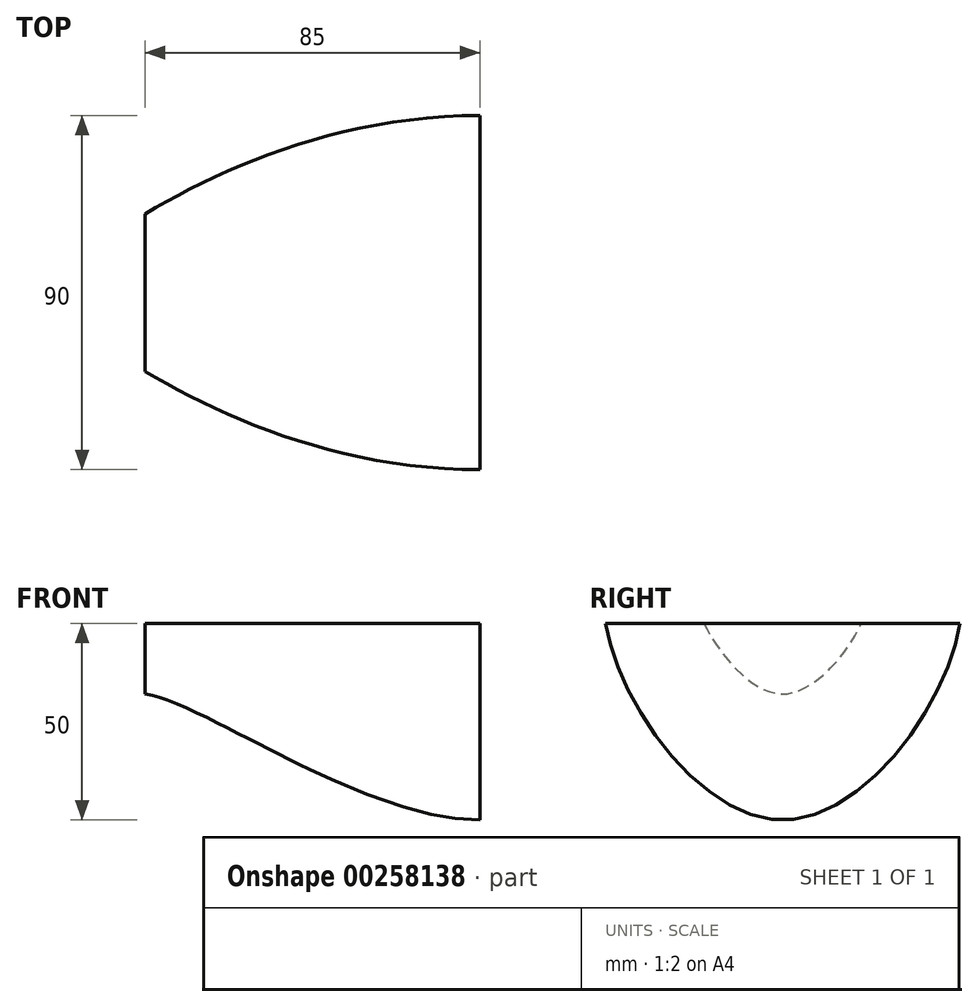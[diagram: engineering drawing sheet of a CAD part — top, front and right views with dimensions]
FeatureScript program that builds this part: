
annotation { "Feature Type Name" : "Feature", "Feature Type Description" : "" }
export const myFeature = defineFeature(function(context is Context, id is Id, definition is map)
    precondition{}
    {
        {
            var Q0;
            Q0=qCreatedBy(makeId("Right.planeOp"),FACE);
            cPlane(context, id + "F0", {"entities" : qUnion([Q0]), "cplaneType" : CPlaneType.OFFSET, "offset" : 85 * mm, "oppositeDirection" : true, "width" : 150 * mm, "height" : 150 * mm});
        }
        {
            var Q0;
            Q0=qCreatedBy(id+"F0.planeOp",FACE);
            var sketch = newSketch(context, id + "F1", { "sketchPlane" : qUnion([Q0])});
            skLineSegment(sketch, "E0", {"start": v(-20, 0) * mm, "end": v(20, 0) * mm});
            skFitSpline(sketch, "E1", {"points": [v(-20, 0) * mm, v(0, -18) * mm, v(20, 0) * mm], "startDerivative": vector(12, -30) * mm, "endDerivative": vector(12, 30) * mm});
            skSolve(sketch);
        }
        {
            var Q0;
            Q0=qCreatedBy(makeId("Right.planeOp"),FACE);
            var sketch = newSketch(context, id + "F2", { "sketchPlane" : qUnion([Q0])});
            skLineSegment(sketch, "E2", {"start": v(-45, 0) * mm, "end": v(45, 0) * mm});
            skFitSpline(sketch, "E3", {"points": [v(-45, 0) * mm, v(0, -50) * mm, v(45, 0) * mm], "startDerivative": vector(18, -120) * mm, "endDerivative": vector(18, 120) * mm});
            skSolve(sketch);
        }
        {
            var Q0;
            Q0=qCreatedBy(makeId("Top.planeOp"),FACE);
            var sketch = newSketch(context, id + "F3", { "sketchPlane" : qUnion([Q0])});
            skFitSpline(sketch, "E4", {"points": [v(-85, 20) * mm, v(0, 45) * mm], "startDerivative": vector(60, 36) * mm, "endDerivative": vector(105, 0) * mm});
            skFitSpline(sketch, "E5.MirrorCS", {"points": [v(-85, -20) * mm, v(0, -45) * mm], "startDerivative": vector(60, -36) * mm, "endDerivative": vector(105, 0) * mm});
            skSolve(sketch);
        }
        {
            var Q0;
            Q0=qCreatedBy(makeId("Front.planeOp"),FACE);
            var sketch = newSketch(context, id + "F4", { "sketchPlane" : qUnion([Q0])});
            skFitSpline(sketch, "E6", {"points": [v(-85, -18) * mm, v(0, -50) * mm], "startDerivative": vector(45, -6) * mm, "endDerivative": vector(89.84, 0) * mm});
            skSolve(sketch);
        }
        {
            var Q0;
            Q0 = qSketchRegion(id + "F1", true);
            var Q1;
            Q1 = qSketchRegion(id + "F2", true);
            var Q2;
            Q2=sQuery(id+"F4.wireOp",EDGE,"E6");
            var Q3;
            Q3=sQuery(id+"F3.wireOp",EDGE,"E5.MirrorCS");
            var Q4;
            Q4=sQuery(id+"F3.wireOp",EDGE,"E4");
            loft(context, id + "F5", {"addGuides" : true, "sheetProfilesArray" : [{ "sheetProfileEntities" : qUnion([Q0]) }, { "sheetProfileEntities" : qUnion([Q1]) }], "guidesArray" : [{ "guideEntities" : qUnion([Q2]), "guideDerivativeType" : LoftGuideDerivativeType.DEFAULT, "guideDerivativeMagnitude" : 1 }, { "guideEntities" : qUnion([Q3]), "guideDerivativeType" : LoftGuideDerivativeType.DEFAULT, "guideDerivativeMagnitude" : 1 }, { "guideEntities" : qUnion([Q4]), "guideDerivativeType" : LoftGuideDerivativeType.DEFAULT, "guideDerivativeMagnitude" : 1 }]});
        }
    });
